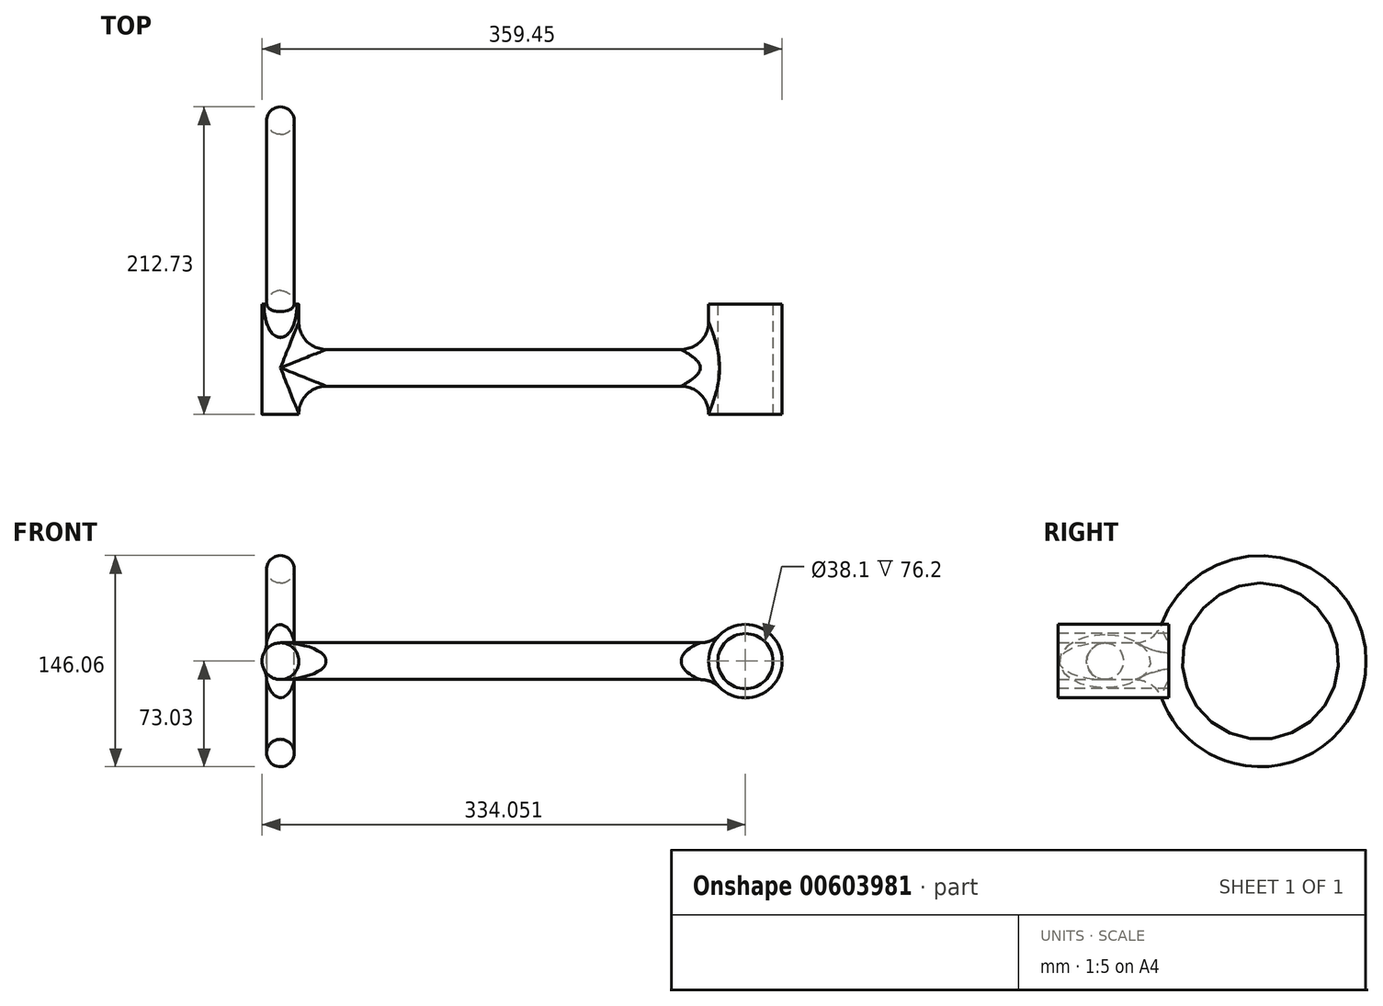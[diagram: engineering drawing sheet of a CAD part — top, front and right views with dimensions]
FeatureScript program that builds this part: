
annotation { "Feature Type Name" : "Feature", "Feature Type Description" : "" }
export const myFeature = defineFeature(function(context is Context, id is Id, definition is map)
    precondition{}
    {
        {
            var Q0;
            Q0=qCreatedBy(makeId("Front.planeOp"),FACE);
            var sketch = newSketch(context, id + "F0", { "sketchPlane" : qUnion([Q0])});
            skCircle(sketch, "E0", {"center": v(0, 0) * mm, "radius": 12.7 * mm});
            skCircle(sketch, "E1", {"center": v(321.35, 0) * mm, "radius": 25.4 * mm});
            skSolve(sketch);
        }
        {
            var Q0;
            Q0 = qSketchRegion(id + "F0", true);
            extrude(context, id + "F1", {"entities" : qUnion([Q0]), "depth" : 76.2 * mm, "offsetDistance" : 25.4 * mm});
        }
        {
            var Q0;
            Q0=qCreatedBy(makeId("Right.planeOp"),FACE);
            var sketch = newSketch(context, id + "F2", { "sketchPlane" : qUnion([Q0])});
            skCircle(sketch, "E2", {"center": v(-43.91, 0) * mm, "radius": 12.7 * mm});
            skSolve(sketch);
        }
        {
            var Q0;
            Q0 = qSketchRegion(id + "F2", true);
            extrude(context, id + "F3", {"entities" : qUnion([Q0]), "operationType" : NewBodyOperationType.ADD, "depth" : 304.8 * mm, "offsetDistance" : 25.4 * mm});
        }
        {
            var Q0;
            Q0=qCreatedBy(makeId("Right.planeOp"),FACE);
            var sketch = newSketch(context, id + "F4", { "sketchPlane" : qUnion([Q0])});
            skCircle(sketch, "E3", {"center": v(63.5, 0) * mm, "radius": 63.5 * mm});
            skSolve(sketch);
        }
        {
            var Q0;
            Q0=qCreatedBy(makeId("Top.planeOp"),FACE);
            var sketch = newSketch(context, id + "F5", { "sketchPlane" : qUnion([Q0])});
            skCircle(sketch, "E4", {"center": v(0, 0) * mm, "radius": 9.53 * mm});
            skSolve(sketch);
        }
        {
            var Q0;
            Q0=makeQuery(id+"F5.imprint","IMPRINT",FACE,{"disambiguationData":[TD([[makeQuery(id+"F5.imprint","IMPRINT",EDGE,{"derivedFrom":sQuery(id+"F5.wireOp",EDGE,"E4")}),1.0]])]});
            var Q1;
            Q1=sQuery(id+"F4.wireOp",EDGE,"E3");
            revolve(context, id + "F6", {"operationType" : NewBodyOperationType.ADD, "entities" : qUnion([Q0]), "axis" : qUnion([Q1]), "revolveType" : RevolveType.FULL});
        }
        {
            var Q0;
            Q0=makeQuery(id+"F1.opExtrude","CAP_FACE",FACE,{"disambiguationData":[OSD([sQuery(id+"F0.wireOp",EDGE,"E1")])],"isStart":false});
            var sketch = newSketch(context, id + "F7", { "sketchPlane" : qUnion([Q0])});
            skCircle(sketch, "E5", {"center": v(321.35, 0) * mm, "radius": 19.05 * mm});
            skSolve(sketch);
        }
        {
            var Q0;
            Q0 = qSketchRegion(id + "F7", true);
            extrude(context, id + "F8", {"entities" : qUnion([Q0]), "operationType" : NewBodyOperationType.REMOVE, "endBound" : BoundingType.THROUGH_ALL, "oppositeDirection" : true, "depth" : 25.4 * mm, "offsetDistance" : 25.4 * mm});
        }
        {
            var Q0;
            Q0=makeQuery(id+"F6.boolean.opBoolean","INTERSECT",EDGE,{"disambiguationData":[OD(1.0)],"derivedFrom":[makeQuery(id+"F1.opExtrude","SWEPT_FACE",FACE,{"disambiguationData":[OSD([sQuery(id+"F0.wireOp",EDGE,"E0")])]}),makeQuery(id+"F6.opRevolve","SWEPT_FACE",FACE,{"disambiguationData":[OSD([sQuery(id+"F5.wireOp",EDGE,"E4")])]})]});
            var Q1;
            Q1=makeQuery(id+"F6.boolean.opBoolean","INTERSECT",EDGE,{"disambiguationData":[OD(0.0)],"derivedFrom":[makeQuery(id+"F1.opExtrude","SWEPT_FACE",FACE,{"disambiguationData":[OSD([sQuery(id+"F0.wireOp",EDGE,"E0")])]}),makeQuery(id+"F6.opRevolve","SWEPT_FACE",FACE,{"disambiguationData":[OSD([sQuery(id+"F5.wireOp",EDGE,"E4")])]})]});
            var Q2;
            Q2=makeQuery(id+"F3.boolean.opBoolean","INTERSECT",EDGE,{"disambiguationData":[OD(0.0)],"derivedFrom":[makeQuery(id+"F1.opExtrude","SWEPT_FACE",FACE,{"disambiguationData":[OSD([sQuery(id+"F0.wireOp",EDGE,"E0")])]}),makeQuery(id+"F3.opExtrude","SWEPT_FACE",FACE,{"disambiguationData":[OSD([sQuery(id+"F2.wireOp",EDGE,"E2")])]})]});
            var Q3;
            Q3=makeQuery(id+"F3.boolean.opBoolean","INTERSECT",EDGE,{"disambiguationData":[OD(1.0)],"derivedFrom":[makeQuery(id+"F1.opExtrude","SWEPT_FACE",FACE,{"disambiguationData":[OSD([sQuery(id+"F0.wireOp",EDGE,"E0")])]}),makeQuery(id+"F3.opExtrude","SWEPT_FACE",FACE,{"disambiguationData":[OSD([sQuery(id+"F2.wireOp",EDGE,"E2")])]})]});
            var Q4;
            Q4=makeQuery(id+"F3.boolean.opBoolean","INTERSECT",EDGE,{"disambiguationData":[OD(0.0)],"derivedFrom":[makeQuery(id+"F1.opExtrude","SWEPT_FACE",FACE,{"disambiguationData":[OSD([sQuery(id+"F0.wireOp",EDGE,"E1")])]}),makeQuery(id+"F3.opExtrude","SWEPT_FACE",FACE,{"disambiguationData":[OSD([sQuery(id+"F2.wireOp",EDGE,"E2")])]})]});
            var Q5;
            Q5=makeQuery(id+"F3.boolean.opBoolean","INTERSECT",EDGE,{"disambiguationData":[OD(1.0)],"derivedFrom":[makeQuery(id+"F1.opExtrude","SWEPT_FACE",FACE,{"disambiguationData":[OSD([sQuery(id+"F0.wireOp",EDGE,"E1")])]}),makeQuery(id+"F3.opExtrude","SWEPT_FACE",FACE,{"disambiguationData":[OSD([sQuery(id+"F2.wireOp",EDGE,"E2")])]})]});
            fillet(context, id + "F9", {"entities" : qUnion([Q0, Q1, Q2, Q3, Q4, Q5]), "radius" : 19.05 * mm, "tangentPropagation" : true, "allowEdgeOverflow" : false});
        }
    });
